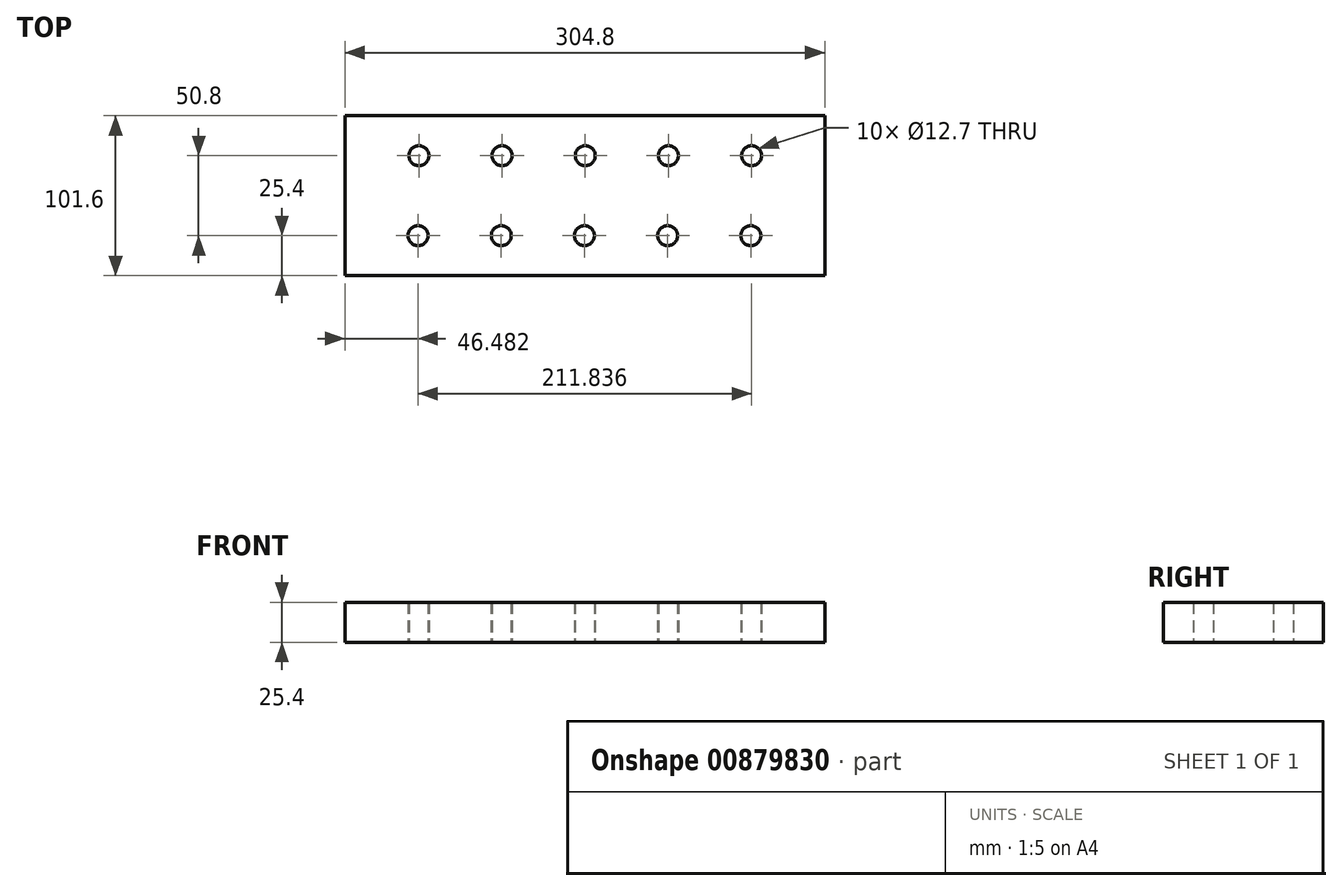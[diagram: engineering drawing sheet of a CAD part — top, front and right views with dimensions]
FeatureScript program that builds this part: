
annotation { "Feature Type Name" : "Feature", "Feature Type Description" : "" }
export const myFeature = defineFeature(function(context is Context, id is Id, definition is map)
    precondition{}
    {
        {
            var Q0;
            Q0=qCreatedBy(makeId("Top.planeOp"),FACE);
            var sketch = newSketch(context, id + "F0", { "sketchPlane" : qUnion([Q0])});
            skLineSegment(sketch, "E0.bottom", {"start": v(0, 0) * mm, "end": v(304.8, 0) * mm});
            skLineSegment(sketch, "E0.top", {"start": v(0, 101.6) * mm, "end": v(304.8, 101.6) * mm});
            skLineSegment(sketch, "E0.left", {"start": v(0, 0) * mm, "end": v(0, 101.6) * mm});
            skLineSegment(sketch, "E0.right", {"start": v(304.8, 0) * mm, "end": v(304.8, 101.6) * mm});
            skCircle(sketch, "E1", {"center": v(46.48, 25.4) * mm, "radius": 6.35 * mm});
            skCircle(sketch, "E2", {"center": v(99.31, 25.4) * mm, "radius": 6.35 * mm});
            skCircle(sketch, "E3", {"center": v(204.98, 25.4) * mm, "radius": 6.35 * mm});
            skCircle(sketch, "E4", {"center": v(205.49, 76.2) * mm, "radius": 6.35 * mm});
            skCircle(sketch, "E5", {"center": v(258.32, 76.2) * mm, "radius": 6.35 * mm});
            skCircle(sketch, "E6", {"center": v(152.15, 25.4) * mm, "radius": 6.35 * mm});
            skCircle(sketch, "E7", {"center": v(99.82, 76.2) * mm, "radius": 6.35 * mm});
            skCircle(sketch, "E8", {"center": v(46.99, 76.2) * mm, "radius": 6.35 * mm});
            skCircle(sketch, "E9", {"center": v(257.81, 25.4) * mm, "radius": 6.35 * mm});
            skCircle(sketch, "E10", {"center": v(152.65, 76.2) * mm, "radius": 6.35 * mm});
            skSolve(sketch);
        }
        {
            var Q0;
            Q0 = qSketchRegion(id + "F0", true);
            extrude(context, id + "F1", {"entities" : qUnion([Q0]), "depth" : 25.4 * mm, "offsetDistance" : 25.4 * mm});
        }
    });
